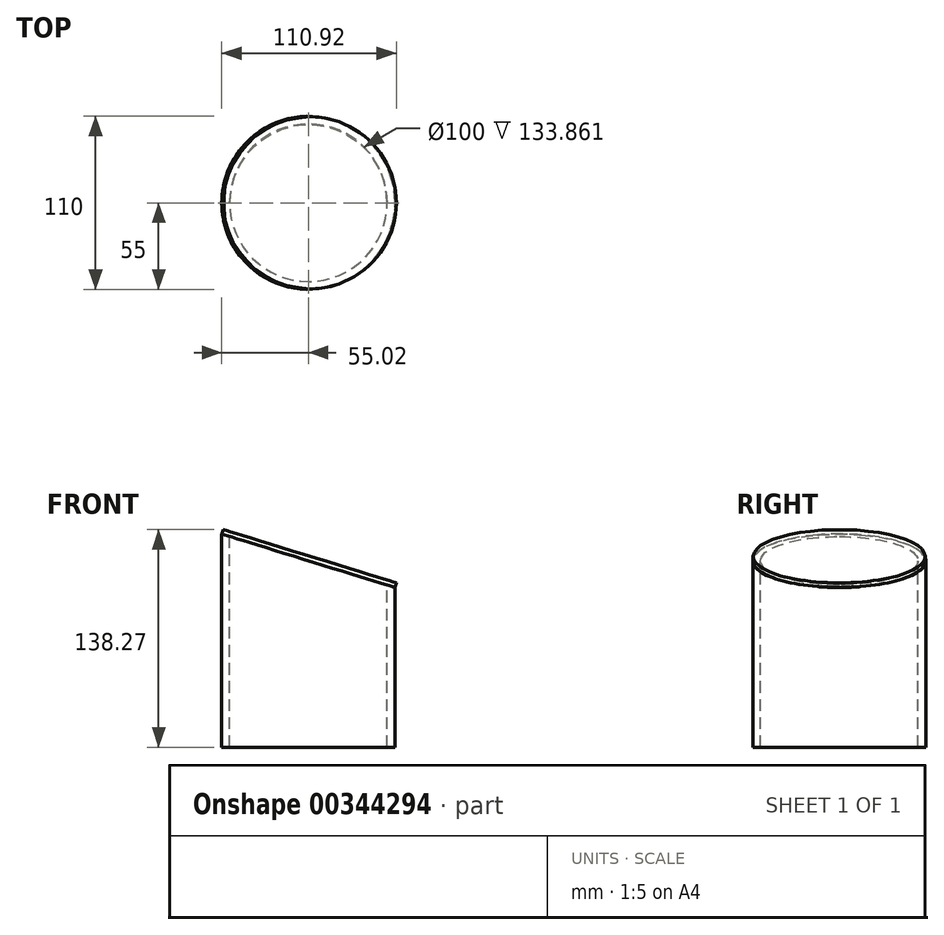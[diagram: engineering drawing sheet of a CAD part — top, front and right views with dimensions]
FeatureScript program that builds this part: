
annotation { "Feature Type Name" : "Feature", "Feature Type Description" : "" }
export const myFeature = defineFeature(function(context is Context, id is Id, definition is map)
    precondition{}
    {
        {
            var Q0;
            Q0=qCreatedBy(makeId("Top.planeOp"),FACE);
            var sketch = newSketch(context, id + "F0", { "sketchPlane" : qUnion([Q0])});
            skCircle(sketch, "E0", {"center": v(0, 0) * mm, "radius": 55 * mm});
            skSolve(sketch);
        }
        {
            var Q0;
            Q0=makeQuery(id+"F0.imprint","IMPRINT",FACE,{"disambiguationData":[TD([[makeQuery(id+"F0.imprint","IMPRINT",EDGE,{"derivedFrom":sQuery(id+"F0.wireOp",EDGE,"E0")}),1.0]])]});
            extrude(context, id + "F1", {"entities" : qUnion([Q0]), "depth" : 145 * mm});
        }
        {
            var Q0;
            Q0=makeQuery(id+"F1.opExtrude","CAP_FACE",FACE,{"disambiguationData":[OSD([sQuery(id+"F0.wireOp",EDGE,"E0")])],"isStart":false});
            var sketch = newSketch(context, id + "F2", { "sketchPlane" : qUnion([Q0])});
            skCircle(sketch, "E1", {"center": v(0, 0) * mm, "radius": 50 * mm});
            skSolve(sketch);
        }
        {
            var Q0;
            Q0=makeQuery(id+"F2.imprint","IMPRINT",FACE,{"disambiguationData":[TD([[makeQuery(id+"F2.imprint","IMPRINT",EDGE,{"derivedFrom":sQuery(id+"F2.wireOp",EDGE,"E1")}),1.0]])]});
            extrude(context, id + "F3", {"entities" : qUnion([Q0]), "operationType" : NewBodyOperationType.REMOVE, "oppositeDirection" : true, "depth" : 145 * mm});
        }
        {
            var Q0;
            Q0=qCreatedBy(makeId("Front.planeOp"),FACE);
            cPlane(context, id + "F4", {"entities" : qUnion([Q0]), "cplaneType" : CPlaneType.OFFSET, "offset" : 100 * mm, "width" : 150 * mm, "height" : 150 * mm});
        }
        {
            var Q0;
            Q0=qCreatedBy(id+"F4.planeOp",FACE);
            var sketch = newSketch(context, id + "F5", { "sketchPlane" : qUnion([Q0])});
            skLineSegment(sketch, "E2", {"start": v(-101.95, 149.86) * mm, "end": v(91.04, 90.4) * mm});
            skLineSegment(sketch, "E3", {"start": v(91.04, 90.4) * mm, "end": v(82.81, 161.75) * mm});
            skLineSegment(sketch, "E4", {"start": v(82.81, 161.75) * mm, "end": v(-101.95, 149.86) * mm});
            skSolve(sketch);
        }
        {
            var Q0;
            Q0 = qSketchRegion(id + "F5", true);
            extrude(context, id + "F6", {"entities" : qUnion([Q0]), "operationType" : NewBodyOperationType.REMOVE, "endBound" : BoundingType.THROUGH_ALL, "oppositeDirection" : true, "depth" : 25 * mm});
        }
        {
            var Q0;
            Q0=makeQuery(id+"F6.boolean.opBoolean","COPY",FACE,{"derivedFrom":makeQuery(id+"F6.opExtrude","SWEPT_FACE",FACE,{"disambiguationData":[OSD([sQuery(id+"F5.wireOp",EDGE,"E2")])]})});
            var sketch = newSketch(context, id + "F7", { "sketchPlane" : qUnion([Q0])});
            skEllipse(sketch, "E5", {"center": v(-34.87, 0) * mm, "majorRadius": 57.57 * mm, "minorRadius": 54.68 * mm, "majorAxis": v(1, 0)});
            skSolve(sketch);
        }
        {
            var Q0;
            Q0 = qSketchRegion(id + "F7", true);
            extrude(context, id + "F8", {"entities" : qUnion([Q0]), "operationType" : NewBodyOperationType.ADD, "depth" : 3 * mm});
        }
    });
